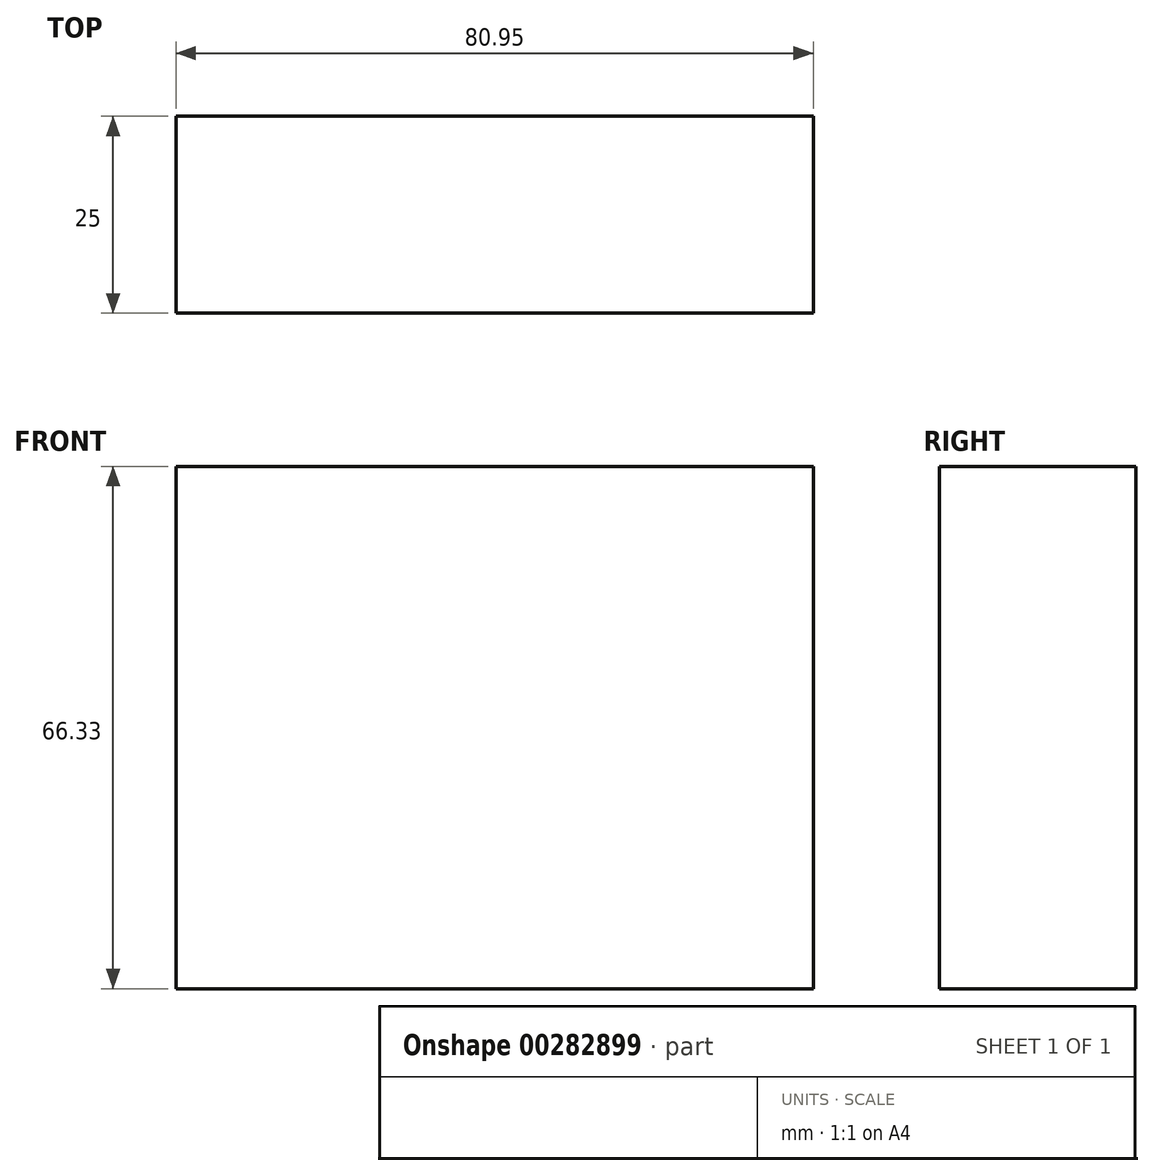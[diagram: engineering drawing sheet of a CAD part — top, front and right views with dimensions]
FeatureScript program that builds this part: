
annotation { "Feature Type Name" : "Feature", "Feature Type Description" : "" }
export const myFeature = defineFeature(function(context is Context, id is Id, definition is map)
    precondition{}
    {
        {
            var Q0;
            Q0=qCreatedBy(makeId("Front.planeOp"),FACE);
            var sketch = newSketch(context, id + "F0", { "sketchPlane" : qUnion([Q0])});
            skLineSegment(sketch, "E0.bottom", {"start": v(-50.6, 2.53) * mm, "end": v(30.36, 2.53) * mm});
            skLineSegment(sketch, "E0.top", {"start": v(-50.6, 68.86) * mm, "end": v(30.36, 68.86) * mm});
            skLineSegment(sketch, "E0.left", {"start": v(-50.6, 2.53) * mm, "end": v(-50.6, 68.86) * mm});
            skLineSegment(sketch, "E0.right", {"start": v(30.36, 2.53) * mm, "end": v(30.36, 68.86) * mm});
            skPoint(sketch, "E0.middle", {"position": v(-10.12, 35.7) * mm});
            skSolve(sketch);
        }
        {
            var Q0;
            Q0=makeQuery(id+"F0.imprint","IMPRINT",FACE,{"disambiguationData":[TD([[makeQuery(id+"F0.imprint","IMPRINT",EDGE,{"derivedFrom":sQuery(id+"F0.wireOp",EDGE,"E0.bottom")}),1.0]])]});
            extrude(context, id + "F1", {"entities" : qUnion([Q0]), "depth" : 25 * mm});
        }
    });
